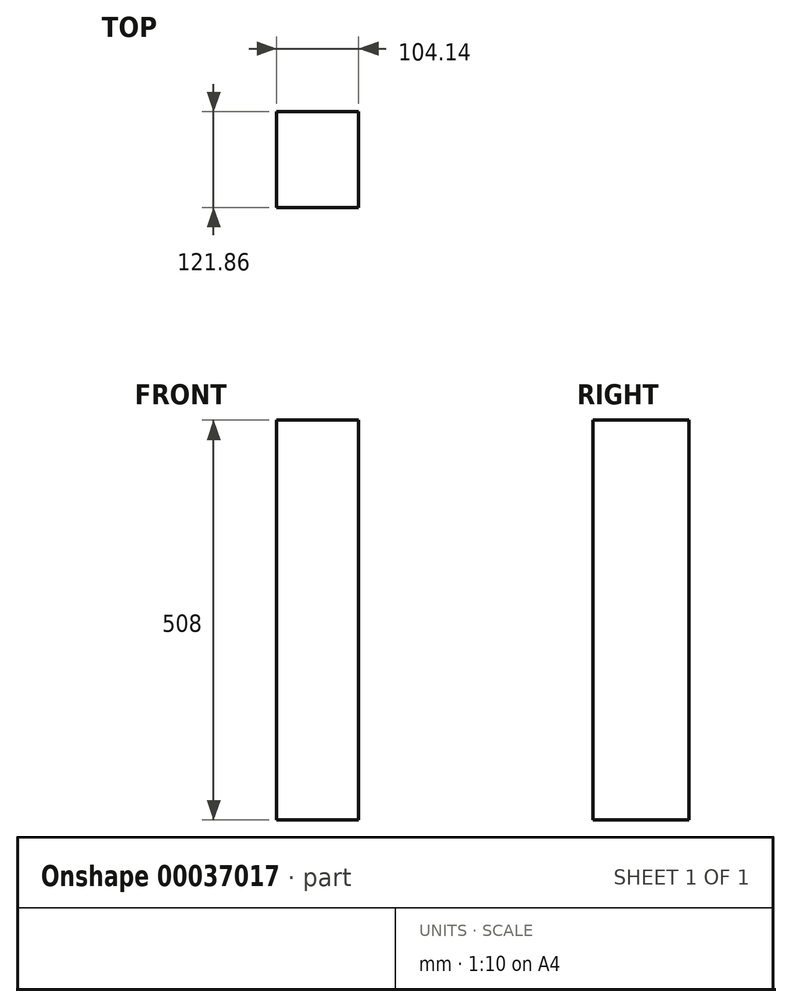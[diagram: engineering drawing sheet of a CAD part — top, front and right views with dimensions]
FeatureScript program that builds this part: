
annotation { "Feature Type Name" : "Feature", "Feature Type Description" : "" }
export const myFeature = defineFeature(function(context is Context, id is Id, definition is map)
    precondition{}
    {
        {
            var Q0;
            Q0=qCreatedBy(makeId("Top.planeOp"),FACE);
            var sketch = newSketch(context, id + "F0", { "sketchPlane" : qUnion([Q0])});
            skLineSegment(sketch, "E0.bottom", {"start": v(0, 0) * mm, "end": v(104.14, 0) * mm});
            skLineSegment(sketch, "E0.top", {"start": v(0, 121.86) * mm, "end": v(104.14, 121.86) * mm});
            skLineSegment(sketch, "E0.left", {"start": v(0, 0) * mm, "end": v(0, 121.86) * mm});
            skLineSegment(sketch, "E0.right", {"start": v(104.14, 0) * mm, "end": v(104.14, 121.86) * mm});
            skSolve(sketch);
        }
        {
            var Q0;
            Q0 = qSketchRegion(id + "F0", true);
            extrude(context, id + "F1", {"entities" : qUnion([Q0]), "depth" : 508 * mm});
        }
    });
